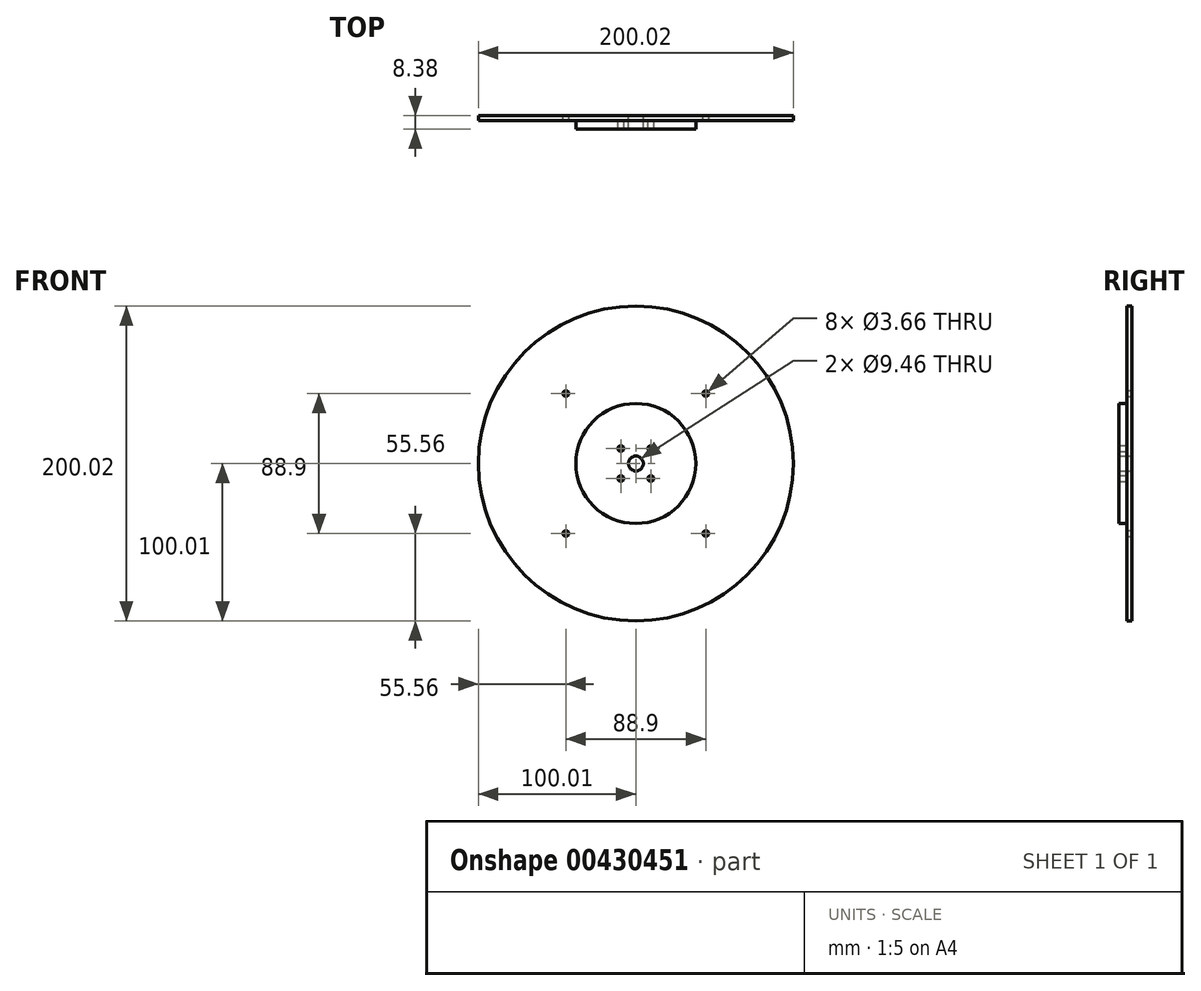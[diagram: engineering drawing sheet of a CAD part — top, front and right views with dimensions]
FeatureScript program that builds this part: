
annotation { "Feature Type Name" : "Feature", "Feature Type Description" : "" }
export const myFeature = defineFeature(function(context is Context, id is Id, definition is map)
    precondition{}
    {
        {
            var Q0;
            Q0=qCreatedBy(makeId("Front.planeOp"),FACE);
            var sketch = newSketch(context, id + "F0", { "sketchPlane" : qUnion([Q0])});
            skLineSegment(sketch, "E0.bottom", {"start": v(-44.45, 44.45) * mm, "end": v(44.45, 44.45) * mm, "construction": true});
            skLineSegment(sketch, "E0.top", {"start": v(-44.45, -44.45) * mm, "end": v(44.45, -44.45) * mm, "construction": true});
            skLineSegment(sketch, "E0.left", {"start": v(-44.45, 44.45) * mm, "end": v(-44.45, -44.45) * mm, "construction": true});
            skLineSegment(sketch, "E0.right", {"start": v(44.45, 44.45) * mm, "end": v(44.45, -44.45) * mm, "construction": true});
            skCircle(sketch, "E1", {"center": v(44.45, -44.45) * mm, "radius": 1.83 * mm});
            skCircle(sketch, "E2", {"center": v(44.45, 44.45) * mm, "radius": 1.83 * mm});
            skCircle(sketch, "E3", {"center": v(-44.45, 44.45) * mm, "radius": 1.83 * mm});
            skCircle(sketch, "E4", {"center": v(-44.45, -44.45) * mm, "radius": 1.83 * mm});
            skCircle(sketch, "E5", {"center": v(0, 0) * mm, "radius": 100.01 * mm});
            skCircle(sketch, "E6", {"center": v(0, 0) * mm, "radius": 4.73 * mm});
            skSolve(sketch);
        }
        {
            var Q0;
            Q0 = qSketchRegion(id + "F0", true);
            extrude(context, id + "F1", {"entities" : qUnion([Q0]), "depth" : 3.17 * mm});
        }
        {
            var Q0;
            Q0=makeQuery(id+"F1.opExtrude","CAP_FACE",FACE,{"disambiguationData":[OSD([sQuery(id+"F0.wireOp",EDGE,"E1"),sQuery(id+"F0.wireOp",EDGE,"E2"),sQuery(id+"F0.wireOp",EDGE,"E3"),sQuery(id+"F0.wireOp",EDGE,"E4"),sQuery(id+"F0.wireOp",EDGE,"E5"),sQuery(id+"F0.wireOp",EDGE,"E6")])],"isStart":false});
            var sketch = newSketch(context, id + "F2", { "sketchPlane" : qUnion([Q0])});
            skCircle(sketch, "E7.0", {"center": v(0, 0) * mm, "radius": 4.73 * mm});
            skCircle(sketch, "E8", {"center": v(0, 0) * mm, "radius": 38.1 * mm});
            skLineSegment(sketch, "E9.bottom", {"start": v(-9.53, 9.52) * mm, "end": v(9.52, 9.53) * mm, "construction": true});
            skLineSegment(sketch, "E9.top", {"start": v(-9.53, -9.52) * mm, "end": v(9.52, -9.52) * mm, "construction": true});
            skLineSegment(sketch, "E9.left", {"start": v(-9.53, 9.52) * mm, "end": v(-9.53, -9.53) * mm, "construction": true});
            skLineSegment(sketch, "E9.right", {"start": v(9.52, 9.53) * mm, "end": v(9.52, -9.52) * mm, "construction": true});
            skCircle(sketch, "E10", {"center": v(9.52, 9.53) * mm, "radius": 1.83 * mm});
            skCircle(sketch, "E11", {"center": v(-9.53, 9.52) * mm, "radius": 1.83 * mm});
            skCircle(sketch, "E12", {"center": v(-9.53, -9.52) * mm, "radius": 1.83 * mm});
            skCircle(sketch, "E13", {"center": v(9.52, -9.52) * mm, "radius": 1.83 * mm});
            skSolve(sketch);
        }
        {
            var Q0;
            Q0=makeQuery(id+"F2.imprint","IMPRINT",FACE,{"disambiguationData":[TD([[makeQuery(id+"F2.imprint","IMPRINT",EDGE,{"derivedFrom":sQuery(id+"F2.wireOp",EDGE,"E7.0")}),-1.0]])]});
            extrude(context, id + "F3", {"entities" : qUnion([Q0]), "depth" : 5.2 * mm});
        }
    });
